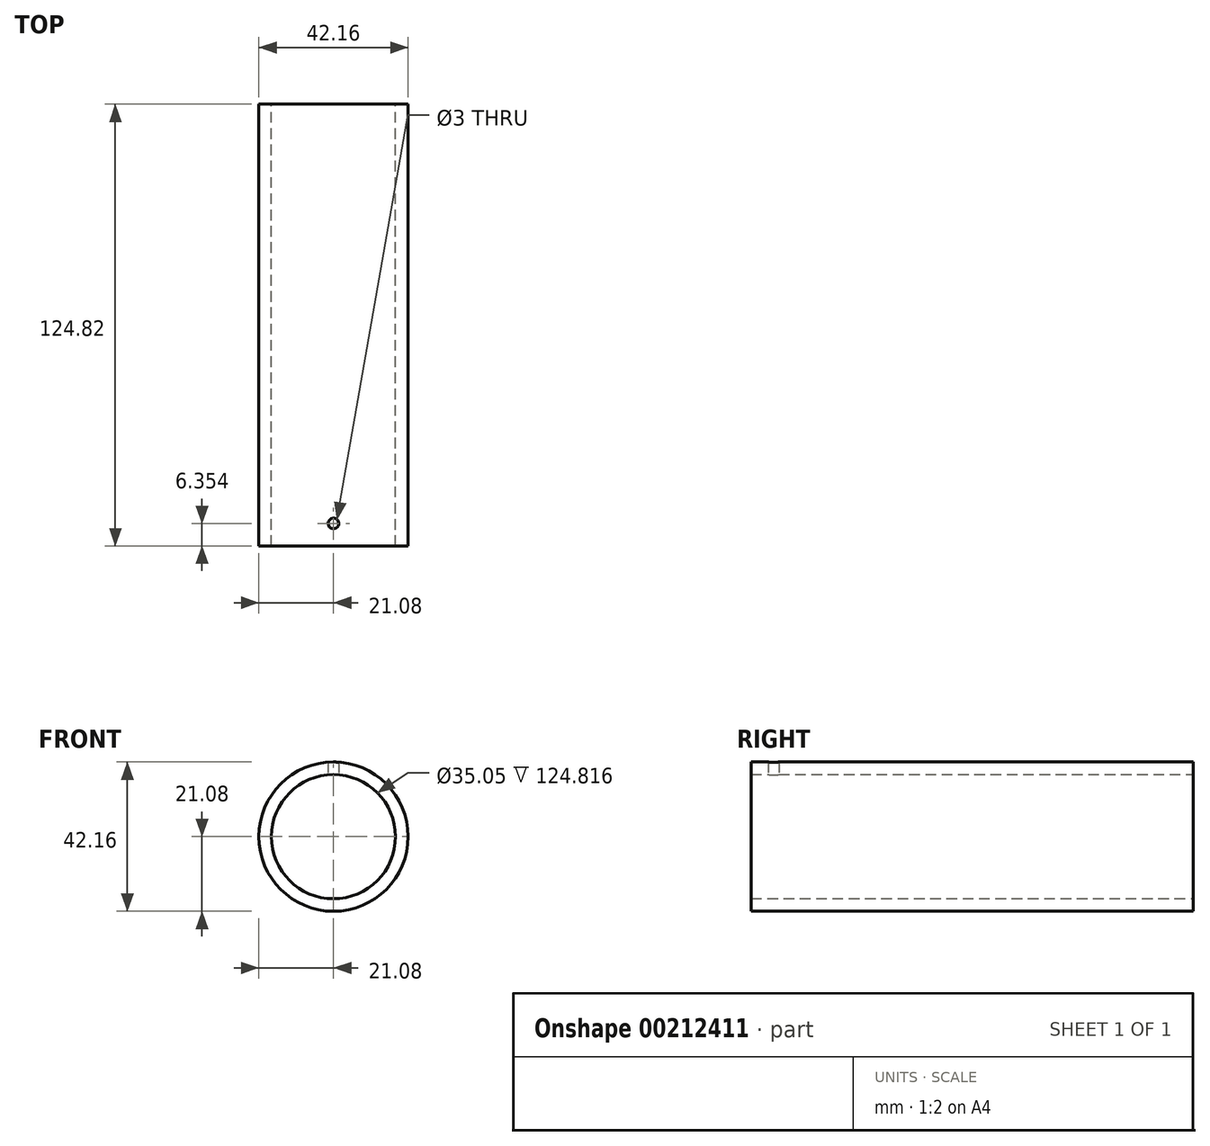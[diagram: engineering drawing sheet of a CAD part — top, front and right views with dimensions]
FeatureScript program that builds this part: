
annotation { "Feature Type Name" : "Feature", "Feature Type Description" : "" }
export const myFeature = defineFeature(function(context is Context, id is Id, definition is map)
    precondition{}
    {
        {
            var Q0;
            Q0=qCreatedBy(makeId("Front.planeOp"),FACE);
            var sketch = newSketch(context, id + "F0", { "sketchPlane" : qUnion([Q0])});
            skCircle(sketch, "E0", {"center": v(0, 0) * mm, "radius": 21.08 * mm});
            skCircle(sketch, "E1", {"center": v(0, 0) * mm, "radius": 17.53 * mm});
            skSolve(sketch);
        }
        {
            var Q0;
            Q0=qSketchRegion(id+"F0",true);
            extrude(context, id + "F1", {"entities" : qUnion([Q0]), "depth" : 124.82 * mm});
        }
        {
            var Q0;
            Q0=qCreatedBy(makeId("Top.planeOp"),FACE);
            var sketch = newSketch(context, id + "F2", { "sketchPlane" : qUnion([Q0])});
            skCircle(sketch, "E2", {"center": v(0, -118.47) * mm, "radius": 1.5 * mm});
            skSolve(sketch);
        }
        {
            var Q0;
            Q0 = qSketchRegion(id + "F2", true);
            extrude(context, id + "F3", {"entities" : qUnion([Q0]), "operationType" : NewBodyOperationType.REMOVE, "depth" : 25.4 * mm});
        }
    });
